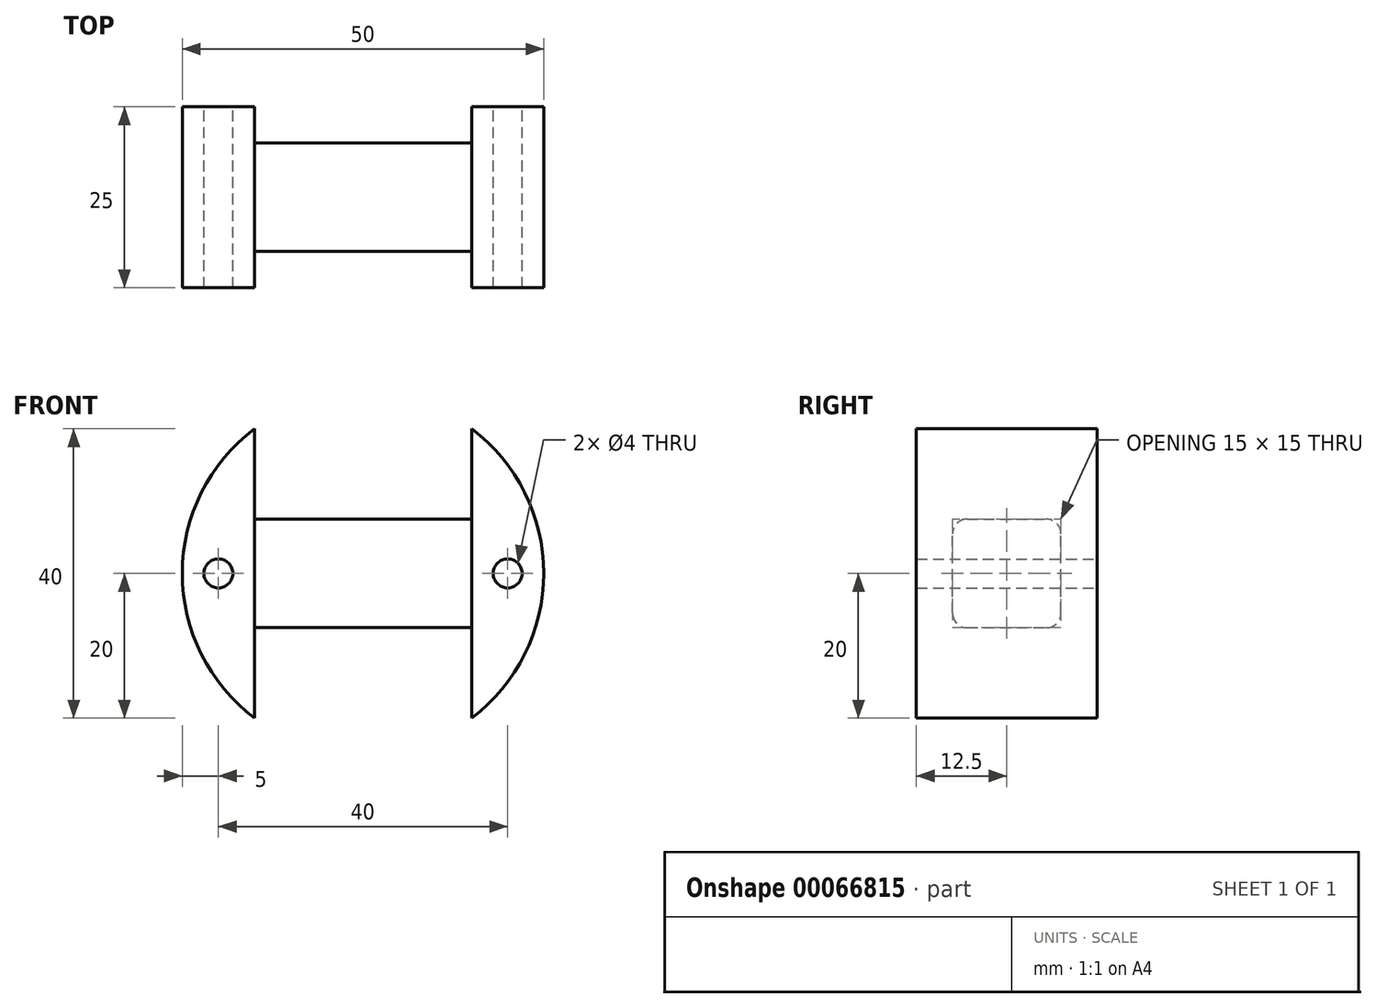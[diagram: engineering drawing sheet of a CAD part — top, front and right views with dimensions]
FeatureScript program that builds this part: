
annotation { "Feature Type Name" : "Feature", "Feature Type Description" : "" }
export const myFeature = defineFeature(function(context is Context, id is Id, definition is map)
    precondition{}
    {
        {
            var Q0;
            Q0=qCreatedBy(makeId("Front.planeOp"),FACE);
            var sketch = newSketch(context, id + "F0", { "sketchPlane" : qUnion([Q0])});
            skArc(sketch, "E0", {"start": v(-15, 20) * mm, "mid": v(-25, 0) * mm, "end": v(-15, -20) * mm});
            skLineSegment(sketch, "E1.top", {"start": v(-15, 7.5) * mm, "end": v(15, 7.5) * mm});
            skLineSegment(sketch, "E1.left", {"start": v(-15, 20) * mm, "end": v(-15, 7.5) * mm});
            skLineSegment(sketch, "E1.right", {"start": v(15, 20) * mm, "end": v(15, 7.5) * mm});
            skLineSegment(sketch, "E2.MirrorCS", {"start": v(-15, -20) * mm, "end": v(-15, -7.5) * mm});
            skLineSegment(sketch, "E3.MirrorCS", {"start": v(15, -20) * mm, "end": v(15, -7.5) * mm});
            skLineSegment(sketch, "E4.MirrorCS", {"start": v(-15, -7.5) * mm, "end": v(15, -7.5) * mm});
            skPoint(sketch, "E1.bottom.end.orphan", {"position": v(15, 32.76) * mm});
            skPoint(sketch, "E5.orphan", {"position": v(-15, 32.76) * mm});
            skPoint(sketch, "E6.orphan", {"position": v(15, -32.76) * mm});
            skPoint(sketch, "E7.MirrorCS.start.orphan", {"position": v(-15, -32.76) * mm});
            skArc(sketch, "E8.trimOffspring", {"start": v(15, -20) * mm, "mid": v(25, 0) * mm, "end": v(15, 20) * mm});
            skLineSegment(sketch, "E9", {"start": v(0, 0) * mm, "end": v(-20, 0) * mm});
            skCircle(sketch, "E10", {"center": v(-20, 0) * mm, "radius": 2 * mm});
            skCircle(sketch, "E11.MirrorC", {"center": v(20, 0) * mm, "radius": 2 * mm});
            skSolve(sketch);
        }
        {
            var Q0;
            Q0=makeQuery(id+"F0.imprint","IMPRINT",FACE,{"disambiguationData":[TD([[makeQuery(id+"F0.imprint","IMPRINT",EDGE,{"derivedFrom":sQuery(id+"F0.wireOp",EDGE,"E0")}),1.0]])]});
            extrude(context, id + "F1", {"entities" : qUnion([Q0]), "depth" : 25 * mm});
        }
        {
            var Q0;
            Q0=qCreatedBy(makeId("Top.planeOp"),FACE);
            var sketch = newSketch(context, id + "F2", { "sketchPlane" : qUnion([Q0])});
            skLineSegment(sketch, "E12.bottom", {"start": v(-15, 7.48) * mm, "end": v(15, 7.48) * mm});
            skLineSegment(sketch, "E12.top", {"start": v(-15, -5) * mm, "end": v(15, -5) * mm});
            skLineSegment(sketch, "E12.left", {"start": v(-15, 7.48) * mm, "end": v(-15, -5) * mm});
            skLineSegment(sketch, "E12.right", {"start": v(15, 7.48) * mm, "end": v(15, -5) * mm});
            skLineSegment(sketch, "E13", {"start": v(-74.79, 0) * mm, "end": v(-74.79, -12.5) * mm});
            skLineSegment(sketch, "E14", {"start": v(-74.79, -12.5) * mm, "end": v(76.03, -12.5) * mm});
            skLineSegment(sketch, "E15.MirrorCS", {"start": v(-15, -32.48) * mm, "end": v(-15, -20) * mm});
            skLineSegment(sketch, "E16.MirrorCS", {"start": v(-15, -32.48) * mm, "end": v(15, -32.48) * mm});
            skLineSegment(sketch, "E17.MirrorCS", {"start": v(15, -32.48) * mm, "end": v(15, -20) * mm});
            skLineSegment(sketch, "E18.MirrorCS", {"start": v(-15, -20) * mm, "end": v(15, -20) * mm});
            skSolve(sketch);
        }
        {
            var Q0;
            Q0=makeQuery(id+"F2.imprint","IMPRINT",FACE,{"disambiguationData":[TD([[makeQuery(id+"F2.imprint","IMPRINT",EDGE,{"derivedFrom":sQuery(id+"F2.wireOp",EDGE,"E12.bottom")}),-1.0]])]});
            var Q1;
            Q1=makeQuery(id+"F2.imprint","IMPRINT",FACE,{"disambiguationData":[TD([[makeQuery(id+"F2.imprint","IMPRINT",EDGE,{"derivedFrom":sQuery(id+"F2.wireOp",EDGE,"E15.MirrorCS")}),-1.0]])]});
            extrude(context, id + "F3", {"entities" : qUnion([Q0, Q1]), "operationType" : NewBodyOperationType.REMOVE, "oppositeDirection" : true, "depth" : 25 * mm, "hasSecondDirection" : true, "secondDirectionOppositeDirection" : false, "secondDirectionDepth" : 25 * mm});
        }
        {
            var Q0;
            Q0=makeQuery(id+"F3.boolean.opBoolean","INTERSECT",EDGE,{"derivedFrom":[makeQuery(id+"F1.opExtrude","SWEPT_FACE",FACE,{"disambiguationData":[OSD([sQuery(id+"F0.wireOp",EDGE,"E1.top")])]}),makeQuery(id+"F3.opExtrude","SWEPT_FACE",FACE,{"disambiguationData":[OSD([sQuery(id+"F2.wireOp",EDGE,"E18.MirrorCS")])]})]});
            var Q1;
            Q1=makeQuery(id+"F3.boolean.opBoolean","INTERSECT",EDGE,{"derivedFrom":[makeQuery(id+"F1.opExtrude","SWEPT_FACE",FACE,{"disambiguationData":[OSD([sQuery(id+"F0.wireOp",EDGE,"E4.MirrorCS")])]}),makeQuery(id+"F3.opExtrude","SWEPT_FACE",FACE,{"disambiguationData":[OSD([sQuery(id+"F2.wireOp",EDGE,"E18.MirrorCS")])]})]});
            var Q2;
            Q2=makeQuery(id+"F3.boolean.opBoolean","INTERSECT",EDGE,{"derivedFrom":[makeQuery(id+"F1.opExtrude","SWEPT_FACE",FACE,{"disambiguationData":[OSD([sQuery(id+"F0.wireOp",EDGE,"E4.MirrorCS")])]}),makeQuery(id+"F3.opExtrude","SWEPT_FACE",FACE,{"disambiguationData":[OSD([sQuery(id+"F2.wireOp",EDGE,"E12.top")])]})]});
            var Q3;
            Q3=makeQuery(id+"F3.boolean.opBoolean","INTERSECT",EDGE,{"derivedFrom":[makeQuery(id+"F1.opExtrude","SWEPT_FACE",FACE,{"disambiguationData":[OSD([sQuery(id+"F0.wireOp",EDGE,"E1.top")])]}),makeQuery(id+"F3.opExtrude","SWEPT_FACE",FACE,{"disambiguationData":[OSD([sQuery(id+"F2.wireOp",EDGE,"E12.top")])]})]});
            fillet(context, id + "F4", {"entities" : qUnion([Q0, Q1, Q2, Q3]), "radius" : 2 * mm, "tangentPropagation" : true, "allowEdgeOverflow" : false});
        }
    });
